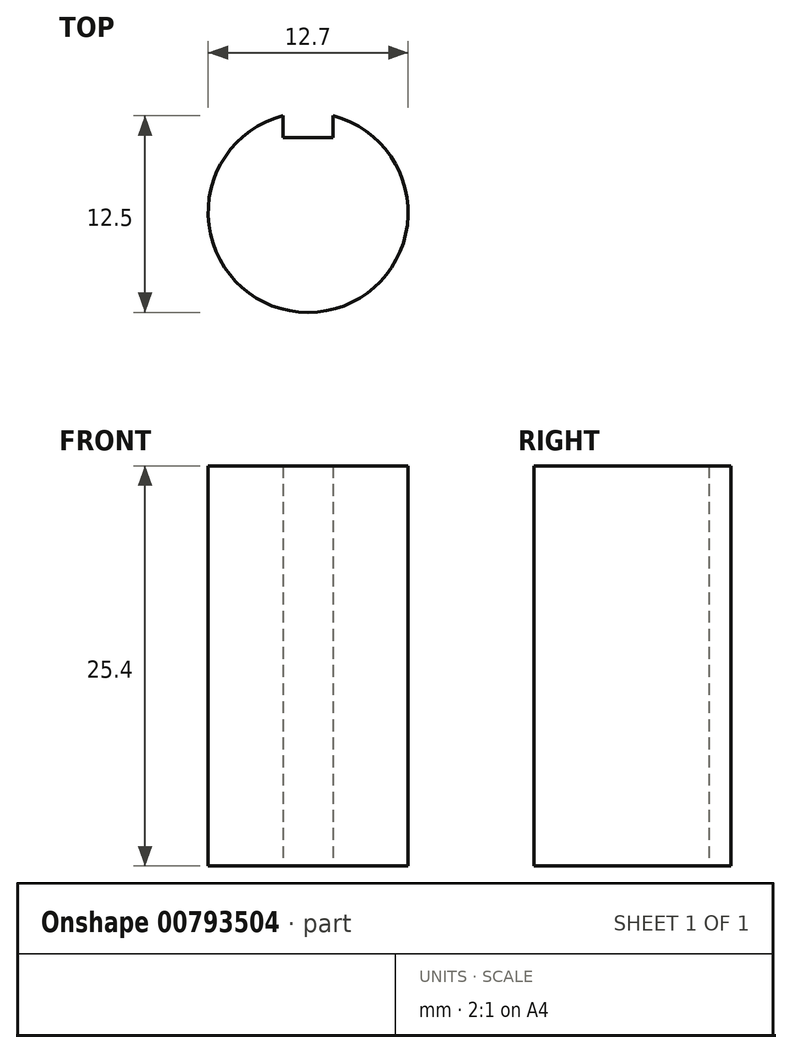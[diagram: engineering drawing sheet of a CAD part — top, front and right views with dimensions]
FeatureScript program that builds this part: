
annotation { "Feature Type Name" : "Feature", "Feature Type Description" : "" }
export const myFeature = defineFeature(function(context is Context, id is Id, definition is map)
    precondition{}
    {
        {
            var Q0;
            Q0=qCreatedBy(makeId("Top.planeOp"),FACE);
            var sketch = newSketch(context, id + "F0", { "sketchPlane" : qUnion([Q0])});
            skCircle(sketch, "E0", {"center": v(0, 0) * mm, "radius": 6.35 * mm});
            skPoint(sketch, "E1", {"position": v(0, 6.35) * mm});
            skLineSegment(sketch, "E2.bottom", {"start": v(-1.59, 7.94) * mm, "end": v(1.59, 7.94) * mm});
            skLineSegment(sketch, "E2.top", {"start": v(-1.59, 4.76) * mm, "end": v(1.59, 4.76) * mm});
            skLineSegment(sketch, "E2.left", {"start": v(-1.59, 7.94) * mm, "end": v(-1.59, 4.76) * mm});
            skLineSegment(sketch, "E2.right", {"start": v(1.59, 7.94) * mm, "end": v(1.59, 4.76) * mm});
            skSolve(sketch);
        }
        {
            var Q0;
            {var subQ5=sQuery(id+"F0.wireOp",EDGE,"E2.top");Q0=makeQuery(id+"F0.imprint","IMPRINT",FACE,{"disambiguationData":[TD([[makeQuery(id+"F0.imprint","IMPRINT",EDGE,{"derivedFrom":subQ5}),-1.0]])]});}
            extrude(context, id + "F1", {"entities" : qUnion([Q0]), "depth" : 25.4 * mm, "offsetDistance" : 25.4 * mm});
        }
    });
